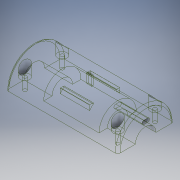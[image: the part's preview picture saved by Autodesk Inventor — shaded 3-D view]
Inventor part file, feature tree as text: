
AUTODESK INVENTOR PART (.ipt)
format: ipt  version: 2018 (Build 220112000, 112)  size: 279,552 bytes
history: native  units: in
note: dims shown in document units (in); Inventor stores cm internally (conversion verified against a paired STEP export)
features: extrude x10, sketch x10, plane x2, fillet x2, mirror x1
ambient origin geometry x8: Origin, YZ Plane, XZ Plane, XY Plane, X Axis, Y Axis, Z Axis, Center Point
bodies: Solid1 (feature_tree)
feature tree (25):
  extrude  "Extrusion1"  Depth=1.0in
  plane  "Work Plane2"
  sketch  "Sketch4"  dims[d29=0.0in d30=0.265in]
  extrude  "Extrusion3"  Depth=0.265in
  extrude  "Extrusion4"  Depth=0.075in TaperAngle=0.0deg
  extrude  "Extrusion5"  Depth=0.5in TaperAngle=0.0deg
  extrude  "Extrusion6"  Depth=1.0in TaperAngle=0.0deg
  extrude  "Extrusion7"  Depth=1.5748in TaperAngle=0.0deg
  extrude  "Extrusion8"  Depth=1.5in TaperAngle=0.0deg
  extrude  "Extrusion9"  Depth=0.5in
  plane  "Work Plane3"
  extrude  "Extrusion10"  Depth=0.5in
  mirror  "Mirror3"
  fillet  "Fillet6"  Radius=0.5in
  fillet  "Fillet7"  Radius=0.19in
  extrude  "Extrusion11"  Depth=1.5in
  sketch  "Sketch1"  dims[d6=1.9685in d7=0.0in d24=1.0in]
  sketch  "Sketch5"  dims[d31=0.075in d34=0.625in d35=0.05in d36=0.0in d37=0.0in]
  sketch  "Sketch6"  dims[d40=0.5in d41=0.5in d42=0.0in]
  sketch  "Sketch7"  dims[d44=1.0in d47=0.5in d48=0.0in]
  sketch  "Sketch9"  dims[d68=0.55in d72=1.5in d73=0.0in]
  sketch  "Sketch10"  dims[d74=0.19in d75=0.5in]
  sketch  "Sketch11"  dims[d76=0.5in d77=0.5in d78=0.5in d79=0.19in]
  sketch  "Sketch12"  dims[d80=0.5in d81=0.5in d82=0.5in d83=0.5in d84=0.19in d85=0.19in d86=1.5in d87=0.0in d88=-1.1196in d89=0.5in d90=0.5in d91=0.5in d92=0.5in d93=0.5in d94=0.5in d95=0.0in d96=0.0in d102=135.0deg d103=0.2in d104=0.1in d105=0.3in d106=0.15in d110=1.5in d111=1.5in d112=1.5in d113=1.5in d114=0.125in d115=0.01in d118=0.55in d119=0.55in d121=0.688in d122=0.2in d123=0.0in d124=0.4in d125=1.0in d126=0.0in d128=0.95in d129=0.95in d130=1.5in d131=0.5in d132=0.5in d133=0.5in]
  sketch  "Sketch8"  dims[d52=1.5in d53=0.0in d61=1.5748in d62=0.0in]
